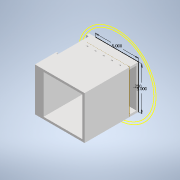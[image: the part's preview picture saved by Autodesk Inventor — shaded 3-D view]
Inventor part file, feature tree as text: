
AUTODESK INVENTOR PART (.ipt)
format: ipt  version: 2022 (Build 260153000, 153)  size: 257,536 bytes
history: native  units: in
note: dims shown in document units (in); Inventor stores cm internally (conversion verified against a paired STEP export)
features: sketch x15, extrude x14, reference x3, projected_geometry x3, other x3, plane x1
ambient origin geometry x8: Origin, YZ Plane, XZ Plane, XY Plane, X Axis, Y Axis, Z Axis, Center Point
bodies: Solid1 (feature_tree)
feature tree (39):
  extrude  "Extrusion1"  Depth=5.0in
  extrude  "Extrusion2"  Depth=0.25in TaperAngle=0.0deg
  extrude  "Extrusion3"  Depth=6.0in TaperAngle=0.0deg
  extrude  "Extrusion4"  Depth=1.5in
  plane  "Work Plane1"
  extrude  "Extrusion5"  Depth=0.25in
  extrude  "Extrusion6"  Depth=0.5in
  extrude  "Extrusion7"  Depth=0.75in
  extrude  "Extrusion8"  Depth=0.25in
  extrude  "Extrusion9"  Depth=0.3937in
  extrude  "Extrusion10"  Depth=0.25in TaperAngle=0.0deg
  sketch  "Sketch12"  dims[d34=0.125in d35=0.125in]
  extrude  "Extrusion11"  Depth=0.125in
  extrude  "Extrusion12"  Depth=4.5in TaperAngle=0.0deg
  extrude  "Extrusion13"  Depth=0.125in TaperAngle=0.0deg
  extrude  "Extrusion14"  Depth=0.875in TaperAngle=0.0deg
  sketch  "Sketch1"  dims[d0=5.0in d1=5.0in]
  reference  "Reference1"
  reference  "Reference2"
  reference  "Reference3"
  sketch  "Sketch2"  dims[d2=0.25in d3=0.25in d4=0.0in]
  sketch  "Sketch3"  dims[d5=0.25in d6=6.0in d7=0.0in]
  projected_geometry  "Projected Loop1"
  sketch  "Sketch4"  dims[d8=0.75in d9=0.0in d10=1.5in]
  sketch  "Sketch6"  dims[d11=4.5in d12=0.25in]
  projected_geometry  "Projected Loop2"
  sketch  "Sketch7"  dims[d13=0.25in d14=0.5in]
  sketch  "Sketch8"  dims[d15=0.3in d16=0.0in d17=0.75in]
  sketch  "Sketch9"  dims[d18=0.25in d19=0.0in d20=0.25in]
  projected_geometry  "Projected Loop3"
  sketch  "Sketch10"  dims[d21=0.5in d22=1.9685in d24=0.95in d25=0.3937in d27=1.0in]
  sketch  "Sketch11"  dims[d29=5.0in d30=0.0in d31=0.25in d32=0.0in]
  sketch  "Sketch13"  dims[d36=10.0in d37=0.0in d38=4.5in d39=0.0in]
  sketch  "Sketch14"  dims[d40=0.125in d41=1.6875in d42=0.0in]
  sketch  "Sketch16"  dims[d43=0.875in d44=0.0in d45=0.875in d46=0.0in]
  sketch  "Sketch17"  dims[d47=4.8125in d48=0.0in d49=4.8125in d50=0.0in]
  other  "<userpath>\OneDrive\Desktop\Smarty Plants Files\Assembly1.iam"
  other  "Assembly1.iam"
  other  "Drainage Base:1"
